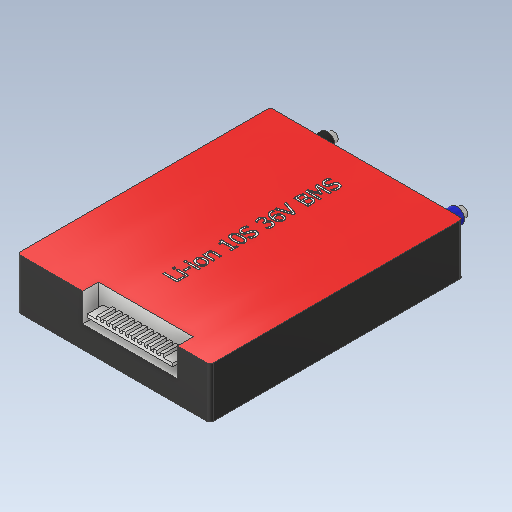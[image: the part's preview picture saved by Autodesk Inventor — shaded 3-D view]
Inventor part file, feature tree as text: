
AUTODESK INVENTOR PART (.ipt)
format: ipt  version: 2020.1 (Build 241239000, 239)  size: 628,736 bytes
history: native  units: mm
features: extrude x5, sketch x4, emboss x1, fillet x1
ambient origin geometry x8: Origin, YZ Plane, XZ Plane, XY Plane, X Axis, Y Axis, Z Axis, Center Point
bodies: Solid1 (feature_tree)
feature tree (11):
  extrude  "Extrusion1"  Depth=80.0mm
  sketch  "Sketch2"  dims[d2=16.0mm d3=0.0mm d4=30.0mm]
  extrude  "Extrusion2"  Depth=16.0mm
  extrude  "Extrusion3"  Depth=1.0mm TaperAngle=0.0deg
  emboss  "Emboss1"
  fillet  "Fillet1"  Radius=1.0mm
  sketch  "Sketch4"  dims[d13=1.0mm d14=0.5mm d15=2.0mm d16=1.0mm d17=2.5mm d18=5.0mm d19=0.0mm d20=3.0mm d21=3.0mm d22=0.1mm d23=0.0mm d24=1.0mm d26=5.0mm d28=10.0mm d29=8.0mm d30=8.0mm d31=0.0mm d32=3.06mm d33=10.0mm d34=0.0mm]
  extrude  "Extrusion4"  Depth=10.0mm
  extrude  "Extrusion5"  Depth=2.0mm
  sketch  "Sketch1"  dims[d0=61.0mm d1=80.0mm]
  sketch  "Sketch3"  dims[d5=5.0mm d6=9.0mm d7=0.0mm d12=1.0mm]
